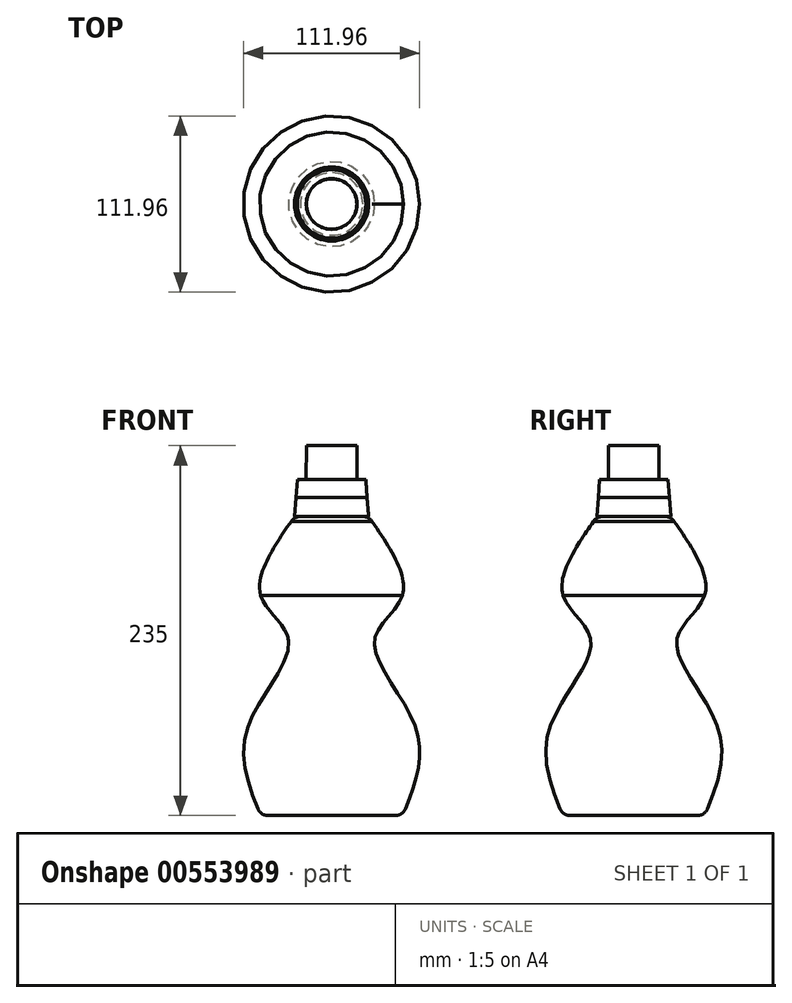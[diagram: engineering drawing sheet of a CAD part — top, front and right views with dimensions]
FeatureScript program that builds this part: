
annotation { "Feature Type Name" : "Feature", "Feature Type Description" : "" }
export const myFeature = defineFeature(function(context is Context, id is Id, definition is map)
    precondition{}
    {
        {
            var Q0;
            Q0=qCreatedBy(makeId("Top.planeOp"),FACE);
            var sketch = newSketch(context, id + "F0", { "sketchPlane" : qUnion([Q0])});
            skCircle(sketch, "E0", {"center": v(0, 0) * mm, "radius": 16 * mm});
            skSolve(sketch);
        }
        {
            var Q0;
            Q0=qCreatedBy(makeId("Top.planeOp"),FACE);
            cPlane(context, id + "F1", {"entities" : qUnion([Q0]), "cplaneType" : CPlaneType.OFFSET, "offset" : 15.5 * mm, "width" : 150 * mm, "height" : 150 * mm});
        }
        {
            var Q0;
            Q0=qCreatedBy(id+"F1.planeOp",FACE);
            var sketch = newSketch(context, id + "F2", { "sketchPlane" : qUnion([Q0])});
            skCircle(sketch, "E1", {"center": v(0, 0) * mm, "radius": 22.5 * mm});
            skSolve(sketch);
        }
        {
            var Q0;
            Q0=qCreatedBy(id+"F1.planeOp",FACE);
            var sketch = newSketch(context, id + "F3", { "sketchPlane" : qUnion([Q0])});
            skCircle(sketch, "E2.0", {"center": v(0, 0) * mm, "radius": 16 * mm});
            skSolve(sketch);
        }
        {
            var Q0;
            Q0=makeQuery(id+"F0.imprint","IMPRINT",FACE,{"disambiguationData":[TD([[makeQuery(id+"F0.imprint","IMPRINT",EDGE,{"derivedFrom":sQuery(id+"F0.wireOp",EDGE,"E0")}),1.0]])]});
            var Q1;
            Q1=makeQuery(id+"F3.imprint","IMPRINT",FACE,{"disambiguationData":[TD([[makeQuery(id+"F3.imprint","IMPRINT",EDGE,{"derivedFrom":sQuery(id+"F3.wireOp",EDGE,"E2.0")}),1.0]])]});
            loft(context, id + "F4", {"sheetProfilesArray" : [{ "sheetProfileEntities" : qUnion([Q0]) }, { "sheetProfileEntities" : qUnion([Q1]) }]});
        }
        {
            var Q0;
            Q0=qCreatedBy(id+"F1.planeOp",FACE);
            cPlane(context, id + "F5", {"entities" : qUnion([Q0]), "cplaneType" : CPlaneType.OFFSET, "offset" : 11.5 * mm, "width" : 150 * mm, "height" : 150 * mm});
        }
        {
            var Q0;
            Q0=qCreatedBy(id+"F5.planeOp",FACE);
            var sketch = newSketch(context, id + "F6", { "sketchPlane" : qUnion([Q0])});
            skCircle(sketch, "E3", {"center": v(0, 0) * mm, "radius": 21.75 * mm});
            skSolve(sketch);
        }
        {
            var Q1;
            Q1=makeQuery(id+"F2.imprint","IMPRINT",FACE,{"disambiguationData":[TD([[makeQuery(id+"F2.imprint","IMPRINT",EDGE,{"derivedFrom":sQuery(id+"F2.wireOp",EDGE,"E1")}),1.0]])]});
            var Q2;
            Q2=makeQuery(id+"F6.imprint","IMPRINT",FACE,{"disambiguationData":[TD([[makeQuery(id+"F6.imprint","IMPRINT",EDGE,{"derivedFrom":sQuery(id+"F6.wireOp",EDGE,"E3")}),1.0]])]});
            loft(context, id + "F7", {"operationType" : NewBodyOperationType.ADD, "sheetProfilesArray" : [{ "sheetProfileEntities" : qUnion([Q1]) }, { "sheetProfileEntities" : qUnion([Q2]) }]});
        }
        {
            var Q0;
            Q0=makeQuery(id+"F7.opLoft","CAP_FACE",FACE,{"disambiguationData":[OSD([makeQuery(id+"F6.imprint","IMPRINT",FACE,{"disambiguationData":[TD([[makeQuery(id+"F6.imprint","IMPRINT",EDGE,{"derivedFrom":sQuery(id+"F6.wireOp",EDGE,"E3")}),1.0]])]})])],"isStart":true});
            var sketch = newSketch(context, id + "F8", { "sketchPlane" : qUnion([Q0])});
            skCircle(sketch, "E4", {"center": v(0, 0) * mm, "radius": 16.1 * mm});
            skSolve(sketch);
        }
        {
            var Q0;
            Q0=qCreatedBy(id+"F5.planeOp",FACE);
            cPlane(context, id + "F9", {"entities" : qUnion([Q0]), "cplaneType" : CPlaneType.OFFSET, "offset" : 21.5 * mm, "width" : 150 * mm, "height" : 150 * mm});
        }
        {
            var Q0;
            Q0=qCreatedBy(id+"F9.planeOp",FACE);
            var sketch = newSketch(context, id + "F10", { "sketchPlane" : qUnion([Q0])});
            skCircle(sketch, "E5", {"center": v(0, 0) * mm, "radius": 16 * mm});
            skSolve(sketch);
        }
        {
            var Q1;
            Q1=makeQuery(id+"F8.imprint","IMPRINT",FACE,{"disambiguationData":[TD([[makeQuery(id+"F8.imprint","IMPRINT",EDGE,{"derivedFrom":sQuery(id+"F8.wireOp",EDGE,"E4")}),1.0]])]});
            var Q2;
            Q2=makeQuery(id+"F10.imprint","IMPRINT",FACE,{"disambiguationData":[TD([[makeQuery(id+"F10.imprint","IMPRINT",EDGE,{"derivedFrom":sQuery(id+"F10.wireOp",EDGE,"E5")}),1.0]])]});
            loft(context, id + "F11", {"operationType" : NewBodyOperationType.ADD, "sheetProfilesArray" : [{ "sheetProfileEntities" : qUnion([Q1]) }, { "sheetProfileEntities" : qUnion([Q2]) }]});
        }
        {
            var Q0;
            Q0=qCreatedBy(id+"F1.planeOp",FACE);
            cPlane(context, id + "F12", {"entities" : qUnion([Q0]), "cplaneType" : CPlaneType.OFFSET, "offset" : 12 * mm, "oppositeDirection" : true, "width" : 150 * mm, "height" : 150 * mm});
        }
        {
            var Q0;
            Q0=qCreatedBy(id+"F12.planeOp",FACE);
            var sketch = newSketch(context, id + "F13", { "sketchPlane" : qUnion([Q0])});
            skCircle(sketch, "E6", {"center": v(0, 0) * mm, "radius": 23.5 * mm});
            skSolve(sketch);
        }
        {
            var Q0;
            Q0=qCreatedBy(makeId("Right.planeOp"),FACE);
            var sketch = newSketch(context, id + "F14", { "sketchPlane" : qUnion([Q0])});
            skLineSegment(sketch, "E7.0", {"start": v(-23.5, 3.5) * mm, "end": v(23.5, 3.5) * mm});
            skPoint(sketch, "E8.0", {"position": v(0, 3.5) * mm});
            skLineSegment(sketch, "E9", {"start": v(0, 3.5) * mm, "end": v(0, -186.5) * mm, "construction": true});
            skSolve(sketch);
        }
        {
            var Q0;
            Q0=qCreatedBy(id+"F12.planeOp",FACE);
            cPlane(context, id + "F15", {"entities" : qUnion([Q0]), "cplaneType" : CPlaneType.OFFSET, "offset" : 190 * mm, "oppositeDirection" : true, "width" : 150 * mm, "height" : 150 * mm});
        }
        {
            var Q0;
            Q0=qCreatedBy(id+"F15.planeOp",FACE);
            var sketch = newSketch(context, id + "F16", { "sketchPlane" : qUnion([Q0])});
            skCircle(sketch, "E10", {"center": v(0, 0) * mm, "radius": 45 * mm});
            skSolve(sketch);
        }
        {
            var Q0;
            Q0=qCreatedBy(id+"F15.planeOp",FACE);
            cPlane(context, id + "F17", {"entities" : qUnion([Q0]), "cplaneType" : CPlaneType.OFFSET, "offset" : 140 * mm, "width" : 150 * mm, "height" : 150 * mm});
        }
        {
            var Q0;
            Q0=qCreatedBy(id+"F17.planeOp",FACE);
            var sketch = newSketch(context, id + "F18", { "sketchPlane" : qUnion([Q0])});
            skCircle(sketch, "E11", {"center": v(0, 0) * mm, "radius": 45 * mm});
            skSolve(sketch);
        }
        {
            var Q0;
            Q0=qCreatedBy(makeId("Right.planeOp"),FACE);
            var sketch = newSketch(context, id + "F19", { "sketchPlane" : qUnion([Q0])});
            skLineSegment(sketch, "E12.0", {"start": v(-45, -46.5) * mm, "end": v(45, -46.5) * mm});
            skLineSegment(sketch, "E13.0", {"start": v(0, 3.5) * mm, "end": v(0, -186.5) * mm});
            skLineSegment(sketch, "E14.0", {"start": v(-23.5, 3.5) * mm, "end": v(23.5, 3.5) * mm});
            skLineSegment(sketch, "E15.0", {"start": v(-45, -186.5) * mm, "end": v(45, -186.5) * mm});
            skPoint(sketch, "E16.0", {"position": v(0, 3.5) * mm});
            skFitSpline(sketch, "E17", {"points": [v(0, 3.5) * mm, v(-23.5, 3.5) * mm], "startDerivative": vector(-23.5, 0) * mm, "endDerivative": vector(-23.5, 0) * mm});
            skFitSpline(sketch, "E18", {"points": [v(-23.5, 3.5) * mm, v(-45, -46.5) * mm, v(-27.22, -75.78) * mm, v(-53.72, -131.5) * mm, v(-45, -186.5) * mm], "startDerivative": vector(-147.75, -212.27) * mm, "endDerivative": vector(85.07, -206.84) * mm});
            skFitSpline(sketch, "E19", {"points": [v(-45, -186.5) * mm, v(0, -186.5) * mm], "startDerivative": vector(45, 0) * mm, "endDerivative": vector(45, 0) * mm});
            skFitSpline(sketch, "E20", {"points": [v(0, -186.5) * mm, v(0, 3.5) * mm], "startDerivative": vector(0, 190) * mm, "endDerivative": vector(0, 190) * mm});
            skSolve(sketch);
        }
        {
            var Q0;
            Q0 = qSketchRegion(id + "F19", true);
            var Q1;
            Q1=sQuery(id+"F16.wireOp",EDGE,"E10");
            sweep(context, id + "F20", {"operationType" : NewBodyOperationType.ADD, "profiles" : qUnion([Q0]), "path" : qUnion([Q1])});
        }
        {
            var Q0;
            Q0=makeQuery(id+"F20.opSweep","SWEPT_EDGE",EDGE,{"disambiguationData":[OSD([sQuery(id+"F16.wireOp",EDGE,"E10"),sQuery(id+"F19.wireOp",EDGE,"E18"),sQuery(id+"F19.wireOp",EDGE,"E19")])]});
            fillet(context, id + "F21", {"entities" : qUnion([Q0]), "radius" : 7 * mm, "tangentPropagation" : true, "allowEdgeOverflow" : false});
        }
        {
            var Q0;
            Q0=qCreatedBy(id+"F12.planeOp",FACE);
            var sketch = newSketch(context, id + "F22", { "sketchPlane" : qUnion([Q0])});
            skCircle(sketch, "E21", {"center": v(0, 0) * mm, "radius": 23.5 * mm});
            skSolve(sketch);
        }
        {
            var Q0;
            Q0=qCreatedBy(id+"F1.planeOp",FACE);
            var sketch = newSketch(context, id + "F23", { "sketchPlane" : qUnion([Q0])});
            skCircle(sketch, "E22", {"center": v(0, 0) * mm, "radius": 22.5 * mm});
            skSolve(sketch);
        }
        {
            var Q1;
            Q1 = qSketchRegion(id + "F22", true);
            var Q2;
            Q2 = qSketchRegion(id + "F23", true);
            loft(context, id + "F24", {"operationType" : NewBodyOperationType.ADD, "sheetProfilesArray" : [{ "sheetProfileEntities" : qUnion([Q1]) }, { "sheetProfileEntities" : qUnion([Q2]) }]});
        }
    });
